# Revit family: Gleitplatte 1x Zoll
name_source: partatom
category: HLS-Bauteile
revit_build: Autodesk Revit 2017 (Build: 20190507_1515(x64)
units: mm (PartAtom-declared; Revit-internal decimal feet)

## family parameters
Arbeitsebenenbasiert = Ja
Beim Laden mit Abzugskörper schneiden = Nein
Bemaßung runder Anschluss = Durchmesser verwenden
Gemeinsam genutzt = Ja
Immer vertikal = Nein
OmniClass-Nummer = 23.75.00.00
OmniClass-Titel = Climate Control (HVAC)
Raumberechnungspunkt = Nein
Teiletyp = Normal

## types (4) — shared parameters
Abstand zur Außenkante = 25 mm  [stored 0.082021 ft]
Firma = MEFA Befestigungs- und Montagesysteme GmbH
Höhe Gewindeanschluss HGW = 15 mm  [stored 0.0492126 ft]
zero-valued in all types: Vorgabe-Ansicht

## per-type parameters (varying)
| type | Anschluss | Anschlüsse | Anzahl Anschlüsse | Artikelnummer | Breite | EAN | Fabrikat | Gewicht | Gewicht pro Bauteil | Kurztext1 | Kurztext2 | Länge | Mengeneinheit | Stärke | max. zul. Last | vpe |
| Gleitplatte 150x100x 8, 1x 1/2" | 1/2'' | Runde Gewindeanschlusse parametrik : Muffe 1/2´´ (0009865) | 1 | 0771200 | 100 mm  [stored 0.328084 ft] | 4250928418227 | MEFA | 0.99 kg | 0.99 kg | Gleitplatte 150 x 100 x 8 | Anschluss 1 x 1/2'' | 150 mm  [stored 0.492126 ft] | St | 8 mm  [stored 0.0262467 ft] | 1.50 kN | 1 St |
| Gleitplatte 150x100x 8, 1x 3/4" | 3/4'' | Runde Gewindeanschlusse parametrik : Schweißmuffe 3/4´´ (0009873) | 1 | 0771227 | 100 mm  [stored 0.328084 ft] | 4250928418258 | MEFA | 1.01 kg | 1.01 kg | Gleitplatte 150 x 100 x 8 | Anschluss 1 x 3/4'' | 150 mm  [stored 0.492126 ft] | St | 8 mm  [stored 0.0262467 ft] | 1.50 kN | 1 St |
| Gleitplatte 350x200x12, 1x 1 1/4" |  | Runde Gewindeanschlusse parametrik : Muffe 1 1/4´´ (0009898) |  | 0771914 | 200 mm  [stored 0.656168 ft] |  |  | 0.00 kg | 0.00 kg |  |  | 350 mm |  | 12 mm  [stored 0.0393701 ft] | 0.00 kN |  |
| Gleitplatte 400x250x12, 1x 1 1/4" |  | Runde Gewindeanschlusse parametrik : Muffe 1 1/4´´ (0009898) |  | 0771975 | 250 mm |  |  | 0.00 kg | 0.00 kg |  |  | 400 mm  [stored 1.31234 ft] |  | 12 mm  [stored 0.0393701 ft] | 0.00 kN |  |

note: [stored X ft] marks values corroborated as IEEE doubles in the binary element streams (Revit-internal decimal feet)

## geometry (parser evidence)
native form markers: Sweep x3
no freeform markers — native parametric forms only
